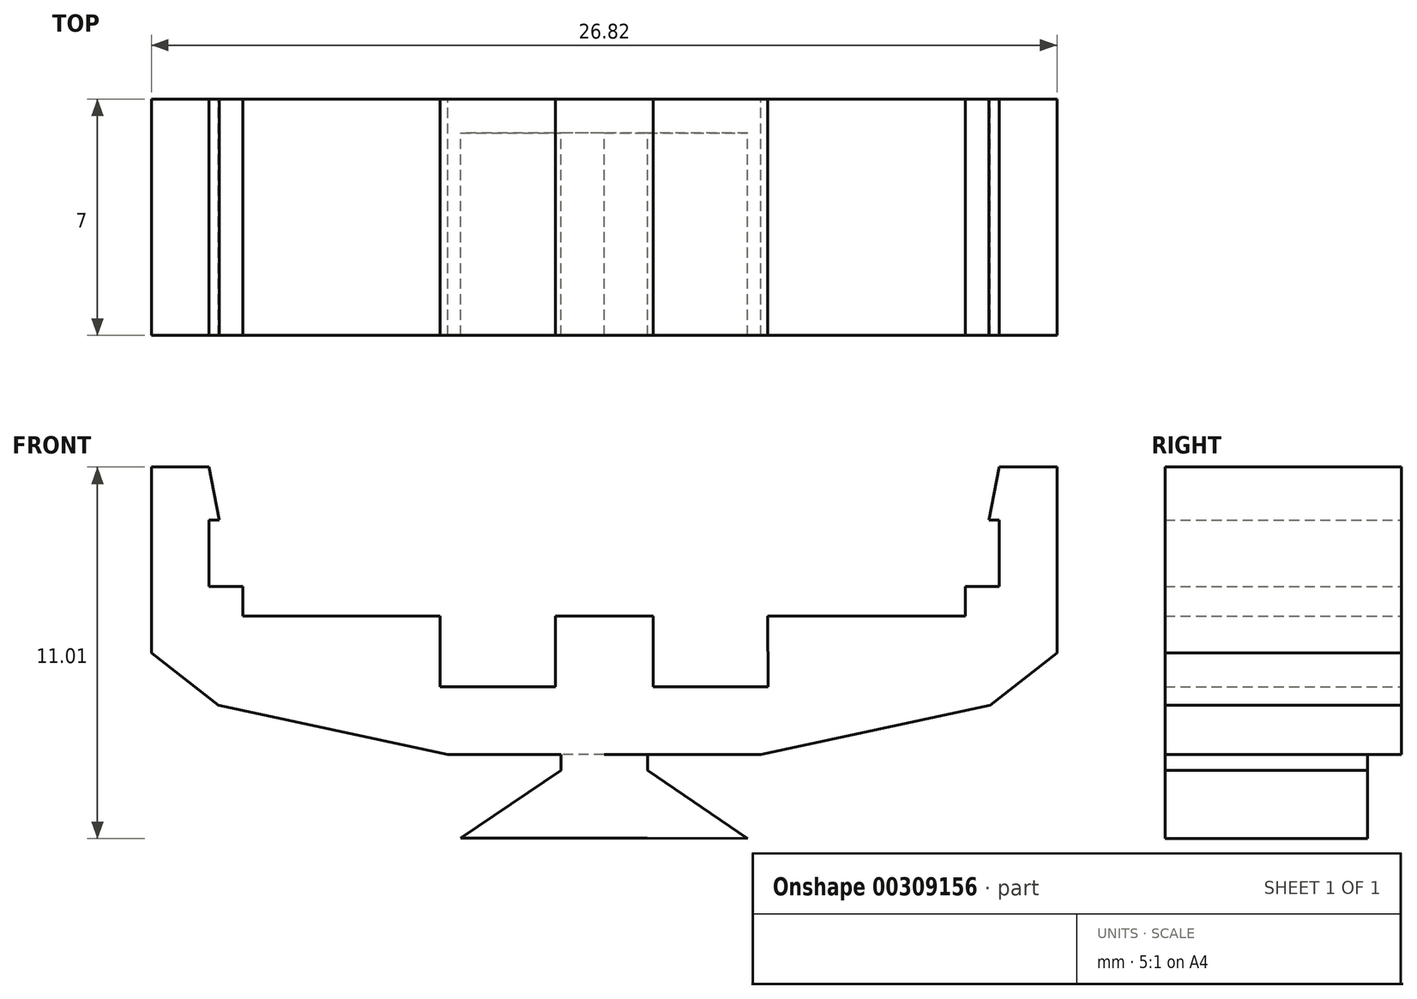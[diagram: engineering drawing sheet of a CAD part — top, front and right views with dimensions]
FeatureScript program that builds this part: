
annotation { "Feature Type Name" : "Feature", "Feature Type Description" : "" }
export const myFeature = defineFeature(function(context is Context, id is Id, definition is map)
    precondition{}
    {
        {
            var Q0;
            Q0=qCreatedBy(makeId("Front.planeOp"),FACE);
            var sketch = newSketch(context, id + "F0", { "sketchPlane" : qUnion([Q0])});
            skLineSegment(sketch, "E0", {"start": v(-2.98, 1.38) * mm, "end": v(-2.98, 1.4) * mm});
            skLineSegment(sketch, "E1", {"start": v(11.7, 5.45) * mm, "end": v(11.7, 6.32) * mm});
            skLineSegment(sketch, "E2", {"start": v(11.7, 8.99) * mm, "end": v(13.41, 8.99) * mm});
            skLineSegment(sketch, "E3", {"start": v(13.41, 3.49) * mm, "end": v(13.41, 8.99) * mm});
            skLineSegment(sketch, "E4.MirrorCS", {"start": v(-13.41, 3.49) * mm, "end": v(-13.41, 8.99) * mm});
            skLineSegment(sketch, "E5.MirrorCS", {"start": v(-11.7, 5.45) * mm, "end": v(-11.7, 6.32) * mm});
            skLineSegment(sketch, "E6.MirrorCS", {"start": v(-11.7, 8.99) * mm, "end": v(-13.41, 8.99) * mm});
            skPoint(sketch, "E7.MirrorCS.end.orphan", {"position": v(-11.65, 1.93) * mm});
            skLineSegment(sketch, "E8", {"start": v(-4.86, 2.47) * mm, "end": v(4.86, 2.47) * mm});
            skLineSegment(sketch, "E9", {"start": v(-10.7, 4.57) * mm, "end": v(-4.86, 4.57) * mm});
            skLineSegment(sketch, "E10", {"start": v(4.84, 4.57) * mm, "end": v(10.7, 4.57) * mm});
            skLineSegment(sketch, "E11", {"start": v(-4.86, 2.47) * mm, "end": v(-4.86, 4.57) * mm});
            skLineSegment(sketch, "E12", {"start": v(4.86, 2.47) * mm, "end": v(4.84, 4.57) * mm});
            skLineSegment(sketch, "E13", {"start": v(11.7, 5.45) * mm, "end": v(11.7, 7.42) * mm});
            skLineSegment(sketch, "E14", {"start": v(11.7, 5.45) * mm, "end": v(10.7, 5.45) * mm});
            skLineSegment(sketch, "E15", {"start": v(10.7, 5.45) * mm, "end": v(10.7, 4.57) * mm});
            skPoint(sketch, "E16.orphan", {"position": v(11.7, 4.57) * mm});
            skLineSegment(sketch, "E17.MirrorCS", {"start": v(-10.7, 5.45) * mm, "end": v(-10.7, 4.57) * mm});
            skLineSegment(sketch, "E18.MirrorCS", {"start": v(-11.7, 5.45) * mm, "end": v(-10.7, 5.45) * mm});
            skLineSegment(sketch, "E19.MirrorCS", {"start": v(-11.7, 5.45) * mm, "end": v(-11.7, 7.42) * mm});
            skPoint(sketch, "E20.orphan", {"position": v(-11.7, 6.32) * mm});
            skPoint(sketch, "E21.orphan", {"position": v(-11.7, 4.57) * mm});
            skLineSegment(sketch, "E22", {"start": v(-11.7, 7.42) * mm, "end": v(-11.7, 8.99) * mm});
            skLineSegment(sketch, "E23", {"start": v(11.7, 7.42) * mm, "end": v(11.7, 8.99) * mm});
            skPoint(sketch, "E24.MirrorCS.start.orphan", {"position": v(-11.7, 7.42) * mm});
            skLineSegment(sketch, "E25", {"start": v(-11.7, 7.42) * mm, "end": v(-11.4, 7.42) * mm});
            skLineSegment(sketch, "E26", {"start": v(-11.4, 7.42) * mm, "end": v(-11.7, 8.99) * mm});
            skLineSegment(sketch, "E27", {"start": v(11.7, 7.42) * mm, "end": v(11.4, 7.42) * mm});
            skLineSegment(sketch, "E28", {"start": v(11.4, 7.42) * mm, "end": v(11.7, 8.99) * mm});
            skLineSegment(sketch, "E29", {"start": v(0, 2.47) * mm, "end": v(0, 4.57) * mm, "construction": true});
            skLineSegment(sketch, "E30", {"start": v(0, 4.57) * mm, "end": v(-1.45, 4.57) * mm});
            skLineSegment(sketch, "E31.MirrorCS", {"start": v(0, 4.57) * mm, "end": v(1.45, 4.57) * mm});
            skLineSegment(sketch, "E32", {"start": v(-1.45, 4.57) * mm, "end": v(-1.45, 2.47) * mm});
            skLineSegment(sketch, "E33", {"start": v(1.45, 4.57) * mm, "end": v(1.45, 2.47) * mm});
            skLineSegment(sketch, "E34", {"start": v(-11.43, 1.93) * mm, "end": v(-4.63, 0.47) * mm});
            skLineSegment(sketch, "E35.MirrorCS", {"start": v(11.43, 1.93) * mm, "end": v(4.63, 0.47) * mm});
            skLineSegment(sketch, "E36", {"start": v(-4.63, 0.47) * mm, "end": v(4.63, 0.47) * mm});
            skLineSegment(sketch, "E37.bottom", {"start": v(0, 0.47) * mm, "end": v(-1.28, 0.47) * mm});
            skLineSegment(sketch, "E37.left", {"start": v(0, 0.47) * mm, "end": v(0, -2) * mm});
            skLineSegment(sketch, "E37.right", {"start": v(-1.28, 0.47) * mm, "end": v(-1.28, -2) * mm});
            skLineSegment(sketch, "E38.bottom", {"start": v(0, 0.47) * mm, "end": v(1.3, 0.47) * mm});
            skLineSegment(sketch, "E38.left", {"start": v(0, 0.47) * mm, "end": v(-0.03, -4.53) * mm});
            skLineSegment(sketch, "E38.right", {"start": v(1.3, 0.47) * mm, "end": v(1.28, -2) * mm});
            skLineSegment(sketch, "E39", {"start": v(1.28, -2) * mm, "end": v(4.25, -2.02) * mm});
            skLineSegment(sketch, "E40", {"start": v(-1.28, -2) * mm, "end": v(-4.25, -2) * mm});
            skLineSegment(sketch, "E41", {"start": v(1.28, -2) * mm, "end": v(-1.28, -2) * mm});
            skPoint(sketch, "E42.MirrorCS.start.orphan", {"position": v(4.25, -4.53) * mm});
            skPoint(sketch, "E43.MirrorCS.start.orphan", {"position": v(1.28, -4.49) * mm});
            skPoint(sketch, "E38.top.end.orphan", {"position": v(1.26, -4.53) * mm});
            skPoint(sketch, "E37.top.start.orphan", {"position": v(0, -4.53) * mm});
            skPoint(sketch, "E44.start.orphan", {"position": v(-1.28, -4.49) * mm});
            skPoint(sketch, "E45.start.orphan", {"position": v(-4.25, -4.53) * mm});
            skLineSegment(sketch, "E46", {"start": v(-4.25, -2) * mm, "end": v(4.25, -2.02) * mm, "construction": true});
            skLineSegment(sketch, "E47", {"start": v(-1.28, 0.47) * mm, "end": v(-1.28, -2) * mm, "construction": true});
            skLineSegment(sketch, "E48", {"start": v(-13.41, 3.49) * mm, "end": v(-11.43, 1.93) * mm});
            skLineSegment(sketch, "E49", {"start": v(11.43, 1.93) * mm, "end": v(13.41, 3.49) * mm});
            skLineSegment(sketch, "E50", {"start": v(-4.25, -2) * mm, "end": v(-1.28, 0) * mm});
            skLineSegment(sketch, "E51", {"start": v(4.25, -2.02) * mm, "end": v(1.29, 0) * mm});
            skLineSegment(sketch, "E52", {"start": v(-1.28, -2) * mm, "end": v(1.28, -2) * mm, "construction": true});
            skLineSegment(sketch, "E53", {"start": v(-4.25, -2) * mm, "end": v(-1.28, -2) * mm, "construction": true});
            skLineSegment(sketch, "E54", {"start": v(-1.28, 0) * mm, "end": v(-1.28, -2) * mm, "construction": true});
            skSolve(sketch);
        }
        {
            var Q0;
            Q0 = qSketchRegion(id + "F0", true);
            extrude(context, id + "F1", {"entities" : qUnion([Q0]), "depth" : 7 * mm});
        }
        {
            var Q0;
            Q0=makeQuery(id+"F1.opExtrude","CAP_FACE",FACE,{"disambiguationData":[OSD([sQuery(id+"F0.wireOp",EDGE,"50951f27-19e4-415f-9534-cca8e01d607a"),sQuery(id+"F0.wireOp",EDGE,"E2"),sQuery(id+"F0.wireOp",EDGE,"E3"),sQuery(id+"F0.wireOp",EDGE,"2c9e5adb-c326-4add-a705-6e4a75ff3a64.MirrorCS"),sQuery(id+"F0.wireOp",EDGE,"E4.MirrorCS"),sQuery(id+"F0.wireOp",EDGE,"E6.MirrorCS"),sQuery(id+"F0.wireOp",EDGE,"E8"),sQuery(id+"F0.wireOp",EDGE,"E9"),sQuery(id+"F0.wireOp",EDGE,"E10"),sQuery(id+"F0.wireOp",EDGE,"E11"),sQuery(id+"F0.wireOp",EDGE,"E12"),sQuery(id+"F0.wireOp",EDGE,"E13"),sQuery(id+"F0.wireOp",EDGE,"E14"),sQuery(id+"F0.wireOp",EDGE,"E15"),sQuery(id+"F0.wireOp",EDGE,"E17.MirrorCS"),sQuery(id+"F0.wireOp",EDGE,"E18.MirrorCS"),sQuery(id+"F0.wireOp",EDGE,"E19.MirrorCS"),sQuery(id+"F0.wireOp",EDGE,"E25"),sQuery(id+"F0.wireOp",EDGE,"E26"),sQuery(id+"F0.wireOp",EDGE,"E27"),sQuery(id+"F0.wireOp",EDGE,"E28"),sQuery(id+"F0.wireOp",EDGE,"E30"),sQuery(id+"F0.wireOp",EDGE,"E31.MirrorCS"),sQuery(id+"F0.wireOp",EDGE,"E32"),sQuery(id+"F0.wireOp",EDGE,"E33"),sQuery(id+"F0.wireOp",EDGE,"E34"),sQuery(id+"F0.wireOp",EDGE,"E35.MirrorCS"),sQuery(id+"F0.wireOp",EDGE,"E36"),sQuery(id+"F0.wireOp",EDGE,"E39"),sQuery(id+"F0.wireOp",EDGE,"ZmNTSwrf-ylrE-1zJi-uYXy-QPSuEQtu8AZO"),sQuery(id+"F0.wireOp",EDGE,"E40"),sQuery(id+"F0.wireOp",EDGE,"qiBHXZsr-i8Pd-Y08x-27rU-iAAU4PR5MIaI"),sQuery(id+"F0.wireOp",EDGE,"E41")])],"isStart":true});
            var sketch = newSketch(context, id + "F2", { "sketchPlane" : qUnion([Q0])});
            skLineSegment(sketch, "E55", {"start": v(-1.3, 0.47) * mm, "end": v(1.28, 0.47) * mm});
            skSolve(sketch);
        }
        {
            var Q0;
            Q0 = qSketchRegion(id + "F2", true);
            var Q1;
            Q1=makeQuery(id+"F2.imprint","IMPRINT",FACE,{"disambiguationData":[TD([[makeQuery(id+"F2.imprint","IMPRINT",EDGE,{"derivedFrom":sQuery(id+"F2.wireOp",EDGE,"E55")}),-1.0]])]});
            extrude(context, id + "F3", {"entities" : qUnion([Q0, Q1]), "operationType" : NewBodyOperationType.REMOVE, "oppositeDirection" : true, "depth" : 1 * mm});
        }
    });
